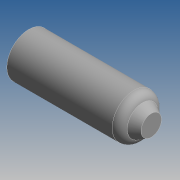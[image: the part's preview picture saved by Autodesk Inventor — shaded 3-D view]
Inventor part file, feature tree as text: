
AUTODESK INVENTOR PART (.ipt)
format: ipt  version: 2019 (Build 230136000, 136)  size: 217,088 bytes
history: native  units: mm
features: revolve x1, fillet x1, sketch x1
ambient origin geometry x8: Origin, YZ Plane, XZ Plane, XY Plane, X Axis, Y Axis, Z Axis, Center Point
bodies: Solid1 (feature_tree)
feature tree (3):
  revolve  "Revolution1"  [1 undecoded]
  fillet  "Fillet2"  Radius=14.0mm
  sketch  "Sketch1"  dims[d0=5.0mm d1=3.5mm d3=14.0mm d4=90.0deg d6=2.0mm d7=60.0deg d8=1.0mm d9=1.0mm]
note: 1 required parameter value undecoded (feature->parameter linkage not recoverable at this tier; creation-order binding heuristic only, values carry confidence <= 0.55)
